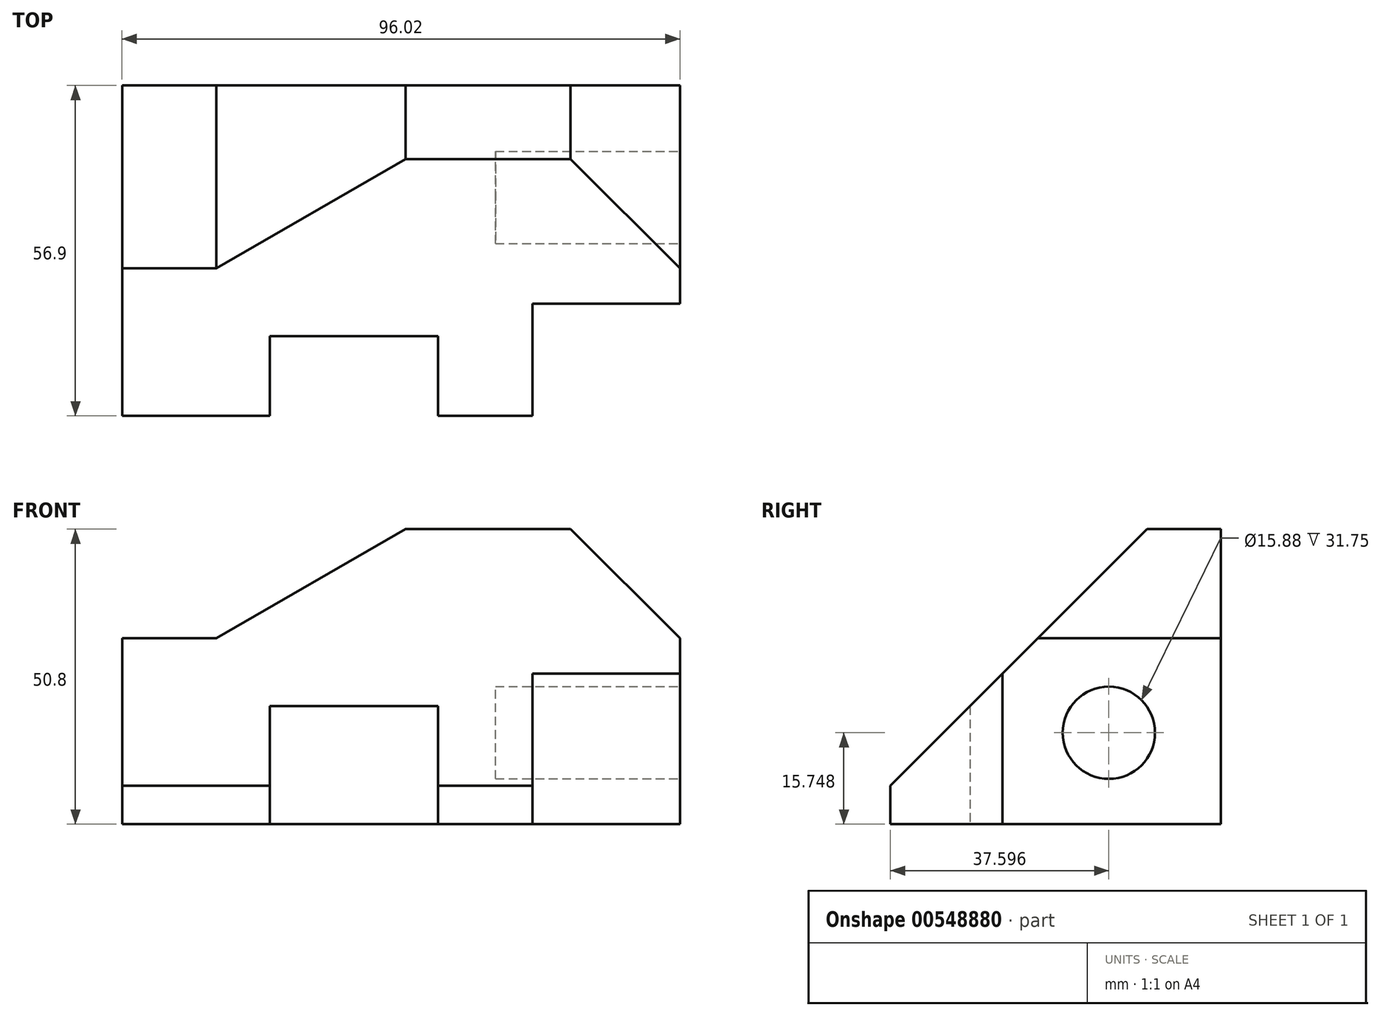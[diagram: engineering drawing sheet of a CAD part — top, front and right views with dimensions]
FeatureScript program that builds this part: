
annotation { "Feature Type Name" : "Feature", "Feature Type Description" : "" }
export const myFeature = defineFeature(function(context is Context, id is Id, definition is map)
    precondition{}
    {
        {
            var Q0;
            Q0=qCreatedBy(makeId("Front.planeOp"),FACE);
            var sketch = newSketch(context, id + "F0", { "sketchPlane" : qUnion([Q0])});
            skLineSegment(sketch, "E0.bottom", {"start": v(-48, 25.4) * mm, "end": v(48, 25.4) * mm});
            skLineSegment(sketch, "E0.top", {"start": v(-48, -25.4) * mm, "end": v(48, -25.4) * mm});
            skLineSegment(sketch, "E0.left", {"start": v(-48, 25.4) * mm, "end": v(-48, -25.4) * mm});
            skLineSegment(sketch, "E0.right", {"start": v(48, 25.4) * mm, "end": v(48, -25.4) * mm});
            skPoint(sketch, "E0.middle", {"position": v(0, 0) * mm});
            skSolve(sketch);
        }
        {
            var Q0;
            Q0 = qSketchRegion(id + "F0", true);
            extrude(context, id + "F1", {"entities" : qUnion([Q0]), "depth" : 56.9 * mm, "offsetDistance" : 25.4 * mm});
        }
        {
            var Q0;
            Q0=makeQuery(id+"F1.opExtrude","SWEPT_FACE",FACE,{"disambiguationData":[OSD([sQuery(id+"F0.wireOp",EDGE,"E0.right")])]});
            var sketch = newSketch(context, id + "F2", { "sketchPlane" : qUnion([Q0])});
            skLineSegment(sketch, "E1", {"start": v(-12.7, 25.4) * mm, "end": v(-56.9, -18.8) * mm});
            skLineSegment(sketch, "E2", {"start": v(-56.9, -18.8) * mm, "end": v(-56.9, 25.4) * mm});
            skLineSegment(sketch, "E3", {"start": v(-56.9, 25.4) * mm, "end": v(-12.7, 25.4) * mm});
            skSolve(sketch);
        }
        {
            var Q0;
            Q0 = qSketchRegion(id + "F2", true);
            extrude(context, id + "F3", {"entities" : qUnion([Q0]), "operationType" : NewBodyOperationType.REMOVE, "endBound" : BoundingType.THROUGH_ALL, "oppositeDirection" : true, "depth" : 25.4 * mm, "offsetDistance" : 25.4 * mm});
        }
        {
            var Q0;
            Q0=makeQuery(id+"F1.opExtrude","CAP_FACE",FACE,{"disambiguationData":[OSD([sQuery(id+"F0.wireOp",EDGE,"E0.bottom"),sQuery(id+"F0.wireOp",EDGE,"E0.top"),sQuery(id+"F0.wireOp",EDGE,"E0.left"),sQuery(id+"F0.wireOp",EDGE,"E0.right")])],"isStart":true});
            var sketch = newSketch(context, id + "F4", { "sketchPlane" : qUnion([Q0])});
            skLineSegment(sketch, "E4", {"start": v(-0.76, 25.4) * mm, "end": v(31.8, 6.6) * mm});
            skLineSegment(sketch, "E5", {"start": v(31.8, 6.6) * mm, "end": v(48, 6.6) * mm});
            skLineSegment(sketch, "E6", {"start": v(48, 6.6) * mm, "end": v(48, 25.4) * mm});
            skLineSegment(sketch, "E7", {"start": v(48, 25.4) * mm, "end": v(-0.76, 25.4) * mm});
            skLineSegment(sketch, "E8", {"start": v(-48, 25.4) * mm, "end": v(-29.21, 25.4) * mm});
            skLineSegment(sketch, "E9", {"start": v(-29.21, 25.4) * mm, "end": v(-48, 6.6) * mm});
            skLineSegment(sketch, "E10", {"start": v(-48, 6.6) * mm, "end": v(-48, 25.4) * mm});
            skSolve(sketch);
        }
        {
            var Q0;
            Q0 = qSketchRegion(id + "F4", true);
            extrude(context, id + "F5", {"entities" : qUnion([Q0]), "operationType" : NewBodyOperationType.REMOVE, "endBound" : BoundingType.THROUGH_ALL, "oppositeDirection" : true, "depth" : 25.4 * mm, "offsetDistance" : 25.4 * mm});
        }
        {
            var Q0;
            Q0=makeQuery(id+"F1.opExtrude","SWEPT_FACE",FACE,{"disambiguationData":[OSD([sQuery(id+"F0.wireOp",EDGE,"E0.top")])]});
            var sketch = newSketch(context, id + "F6", { "sketchPlane" : qUnion([Q0])});
            skLineSegment(sketch, "E11.bottom", {"start": v(-22.6, 56.9) * mm, "end": v(6.35, 56.9) * mm});
            skLineSegment(sketch, "E11.top", {"start": v(-22.6, 43.18) * mm, "end": v(6.35, 43.18) * mm});
            skLineSegment(sketch, "E11.left", {"start": v(-22.6, 56.9) * mm, "end": v(-22.6, 43.18) * mm});
            skLineSegment(sketch, "E11.right", {"start": v(6.35, 56.9) * mm, "end": v(6.35, 43.18) * mm});
            skLineSegment(sketch, "E12.bottom", {"start": v(48, 56.9) * mm, "end": v(22.6, 56.9) * mm});
            skLineSegment(sketch, "E12.top", {"start": v(48, 37.6) * mm, "end": v(22.6, 37.6) * mm});
            skLineSegment(sketch, "E12.left", {"start": v(48, 56.9) * mm, "end": v(48, 37.6) * mm});
            skLineSegment(sketch, "E12.right", {"start": v(22.6, 56.9) * mm, "end": v(22.6, 37.6) * mm});
            skSolve(sketch);
        }
        {
            var Q0;
            Q0 = qSketchRegion(id + "F6", true);
            extrude(context, id + "F7", {"entities" : qUnion([Q0]), "operationType" : NewBodyOperationType.REMOVE, "endBound" : BoundingType.THROUGH_ALL, "oppositeDirection" : true, "depth" : 25.4 * mm, "offsetDistance" : 25.4 * mm});
        }
        {
            var Q0;
            Q0=makeQuery(id+"F1.opExtrude","SWEPT_FACE",FACE,{"disambiguationData":[OSD([sQuery(id+"F0.wireOp",EDGE,"E0.right")])]});
            var sketch = newSketch(context, id + "F8", { "sketchPlane" : qUnion([Q0])});
            skCircle(sketch, "E13", {"center": v(-19.3, -9.65) * mm, "radius": 7.94 * mm});
            skSolve(sketch);
        }
        {
            var Q0;
            Q0 = qSketchRegion(id + "F8", true);
            extrude(context, id + "F9", {"entities" : qUnion([Q0]), "operationType" : NewBodyOperationType.REMOVE, "oppositeDirection" : true, "depth" : 31.75 * mm, "offsetDistance" : 25.4 * mm});
        }
    });
